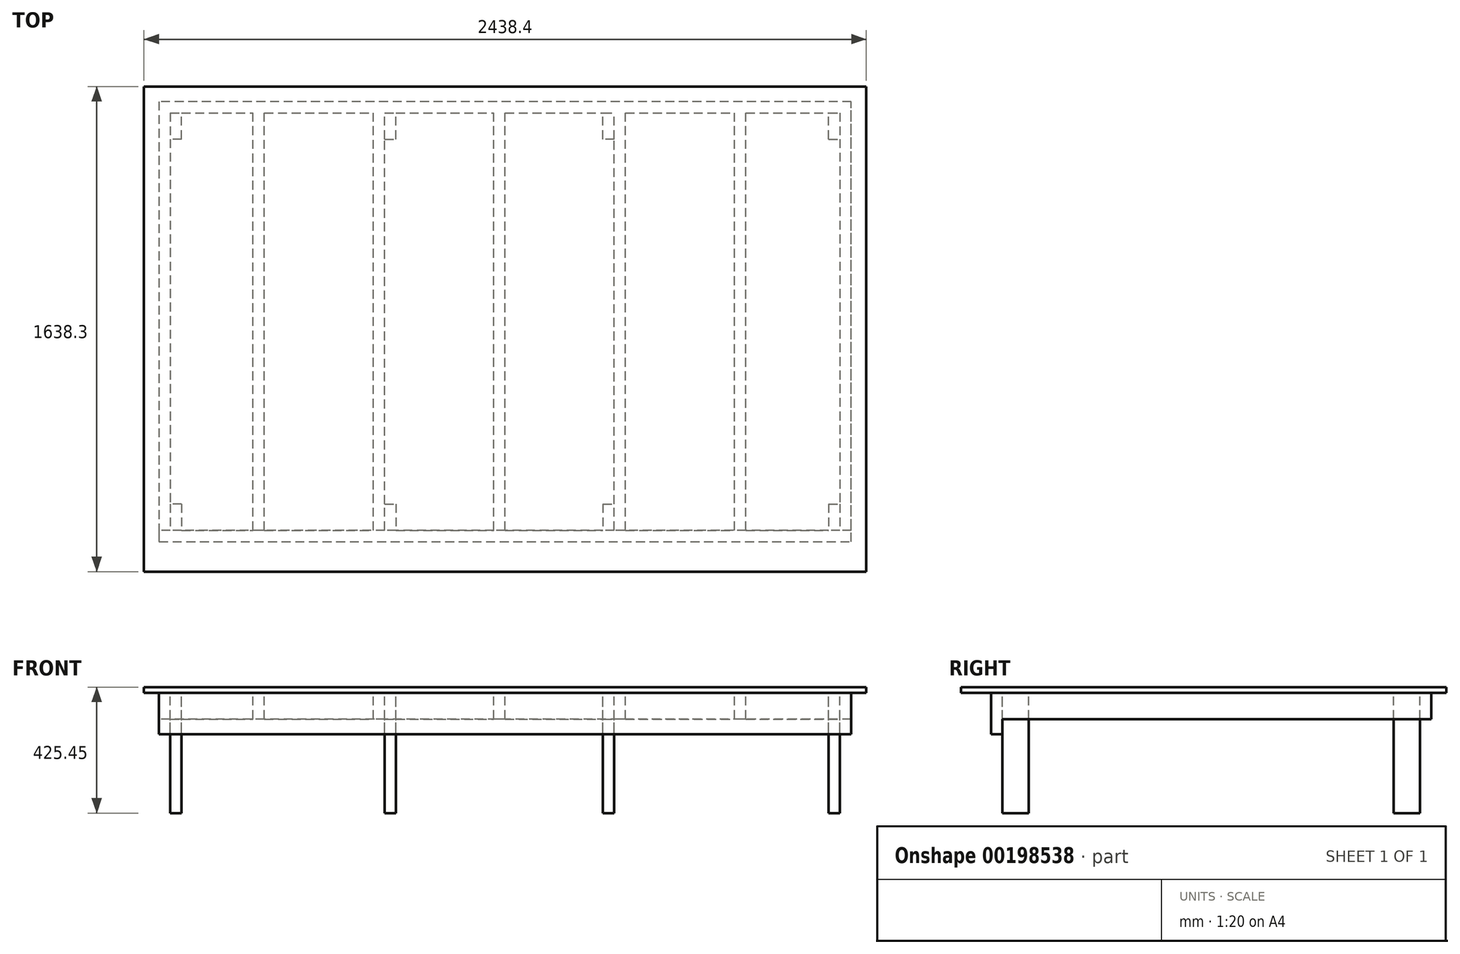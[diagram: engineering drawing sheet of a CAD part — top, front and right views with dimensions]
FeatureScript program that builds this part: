
annotation { "Feature Type Name" : "Feature", "Feature Type Description" : "" }
export const myFeature = defineFeature(function(context is Context, id is Id, definition is map)
    precondition{}
    {
        {
            var Q0;
            Q0=qCreatedBy(makeId("Top.planeOp"),FACE);
            var sketch = newSketch(context, id + "F0", { "sketchPlane" : qUnion([Q0])});
            skLineSegment(sketch, "E0.bottom", {"start": v(0, 0) * mm, "end": v(2438.4, 0) * mm});
            skLineSegment(sketch, "E0.top", {"start": v(0, -1638.3) * mm, "end": v(2438.4, -1638.3) * mm});
            skLineSegment(sketch, "E0.left", {"start": v(0, 0) * mm, "end": v(0, -1638.3) * mm});
            skLineSegment(sketch, "E0.right", {"start": v(2438.4, 0) * mm, "end": v(2438.4, -1638.3) * mm});
            skLineSegment(sketch, "E1", {"start": v(0, -914.4) * mm, "end": v(2438.4, -914.4) * mm});
            skSolve(sketch);
        }
        {
            var Q0;
            Q0 = qSketchRegion(id + "F0", true);
            extrude(context, id + "F1", {"entities" : qUnion([Q0]), "depth" : 19.05 * mm});
        }
        {
            var Q0;
            Q0=makeQuery(id+"F1.opExtrude","CAP_FACE",FACE,{"disambiguationData":[OSD([sQuery(id+"F0.wireOp",EDGE,"E0.bottom"),sQuery(id+"F0.wireOp",EDGE,"E0.top"),sQuery(id+"F0.wireOp",EDGE,"E0.left"),sQuery(id+"F0.wireOp",EDGE,"E0.right")])],"isStart":true});
            var sketch = newSketch(context, id + "F2", { "sketchPlane" : qUnion([Q0])});
            skLineSegment(sketch, "E2.top", {"start": v(88.9, 88.9) * mm, "end": v(368.3, 88.9) * mm});
            skLineSegment(sketch, "E3.top", {"start": v(88.9, 1498.6) * mm, "end": v(368.3, 1498.6) * mm});
            skLineSegment(sketch, "E4", {"start": v(2349.5, 88.9) * mm, "end": v(2349.5, 1498.6) * mm});
            skLineSegment(sketch, "E5", {"start": v(88.9, 88.9) * mm, "end": v(88.9, 1498.6) * mm});
            skLineSegment(sketch, "E6", {"start": v(387.35, 1663.87) * mm, "end": v(387.35, -78) * mm, "construction": true});
            skLineSegment(sketch, "E7", {"start": v(793.75, 1668.2) * mm, "end": v(793.75, -56.39) * mm, "construction": true});
            skLineSegment(sketch, "E8", {"start": v(1200.15, 1668.2) * mm, "end": v(1200.15, -58.55) * mm, "construction": true});
            skLineSegment(sketch, "E9", {"start": v(368.3, 1498.6) * mm, "end": v(368.3, 88.9) * mm});
            skLineSegment(sketch, "E10", {"start": v(774.7, 1498.6) * mm, "end": v(774.7, 88.9) * mm});
            skLineSegment(sketch, "E11.MirrorCS", {"start": v(406.4, 1498.6) * mm, "end": v(406.4, 88.9) * mm});
            skLineSegment(sketch, "E12.MirrorCS", {"start": v(812.8, 1498.6) * mm, "end": v(812.8, 88.9) * mm});
            skLineSegment(sketch, "E13.MirrorCS", {"start": v(1993.9, 1498.6) * mm, "end": v(1993.9, 88.9) * mm});
            skLineSegment(sketch, "E14.MirrorCS", {"start": v(1625.6, 1498.6) * mm, "end": v(1625.6, 88.9) * mm});
            skLineSegment(sketch, "E15.MirrorCS", {"start": v(1587.5, 1498.6) * mm, "end": v(1587.5, 88.9) * mm});
            skLineSegment(sketch, "E16.MirrorCS", {"start": v(2032, 1498.6) * mm, "end": v(2032, 88.9) * mm});
            skLineSegment(sketch, "E17.trimOffspring", {"start": v(1625.6, 1498.6) * mm, "end": v(1993.9, 1498.6) * mm});
            skLineSegment(sketch, "E18.trimOffspring", {"start": v(2032, 1498.6) * mm, "end": v(2349.5, 1498.6) * mm});
            skLineSegment(sketch, "E19.trimOffspring", {"start": v(2032, 88.9) * mm, "end": v(2349.5, 88.9) * mm});
            skLineSegment(sketch, "E20.trimOffspring", {"start": v(1625.6, 88.9) * mm, "end": v(1993.9, 88.9) * mm});
            skLineSegment(sketch, "E21.trimOffspring", {"start": v(812.8, 88.9) * mm, "end": v(1181.1, 88.9) * mm});
            skLineSegment(sketch, "E22.trimOffspring", {"start": v(406.4, 88.9) * mm, "end": v(774.7, 88.9) * mm});
            skLineSegment(sketch, "E23.trimOffspring", {"start": v(406.4, 1498.6) * mm, "end": v(774.7, 1498.6) * mm});
            skLineSegment(sketch, "E24.trimOffspring", {"start": v(812.8, 1498.6) * mm, "end": v(1181.1, 1498.6) * mm});
            skLineSegment(sketch, "E25", {"start": v(1181.1, 1498.6) * mm, "end": v(1181.1, 88.9) * mm});
            skLineSegment(sketch, "E26.MirrorCS", {"start": v(1219.2, 1498.6) * mm, "end": v(1219.2, 88.9) * mm});
            skLineSegment(sketch, "E27.trimOffspring", {"start": v(1219.2, 1498.6) * mm, "end": v(1587.5, 1498.6) * mm});
            skLineSegment(sketch, "E28.trimOffspring", {"start": v(1219.2, 88.9) * mm, "end": v(1587.5, 88.9) * mm});
            skLineSegment(sketch, "E29", {"start": v(50.8, 1536.7) * mm, "end": v(2387.6, 1536.7) * mm});
            skLineSegment(sketch, "E30", {"start": v(2387.6, 1536.7) * mm, "end": v(2387.6, 50.8) * mm});
            skLineSegment(sketch, "E31", {"start": v(2387.6, 50.8) * mm, "end": v(50.8, 50.8) * mm});
            skLineSegment(sketch, "E32", {"start": v(50.8, 50.8) * mm, "end": v(50.8, 1536.7) * mm});
            skSolve(sketch);
        }
        {
            var Q0;
            Q0 = qSketchRegion(id + "F2", true);
            extrude(context, id + "F3", {"entities" : qUnion([Q0]), "operationType" : NewBodyOperationType.ADD, "depth" : 88.9 * mm});
        }
        {
            var Q0;
            Q0=makeQuery(id+"F3.opExtrude","CAP_FACE",FACE,{"disambiguationData":[OSD([sQuery(id+"F2.wireOp",EDGE,"E2.top"),sQuery(id+"F2.wireOp",EDGE,"E3.top"),sQuery(id+"F2.wireOp",EDGE,"E4"),sQuery(id+"F2.wireOp",EDGE,"E5"),sQuery(id+"F2.wireOp",EDGE,"E9"),sQuery(id+"F2.wireOp",EDGE,"E10"),sQuery(id+"F2.wireOp",EDGE,"E11.MirrorCS"),sQuery(id+"F2.wireOp",EDGE,"E12.MirrorCS"),sQuery(id+"F2.wireOp",EDGE,"E13.MirrorCS"),sQuery(id+"F2.wireOp",EDGE,"E14.MirrorCS"),sQuery(id+"F2.wireOp",EDGE,"E15.MirrorCS"),sQuery(id+"F2.wireOp",EDGE,"E16.MirrorCS"),sQuery(id+"F2.wireOp",EDGE,"E17.trimOffspring"),sQuery(id+"F2.wireOp",EDGE,"E18.trimOffspring"),sQuery(id+"F2.wireOp",EDGE,"E19.trimOffspring"),sQuery(id+"F2.wireOp",EDGE,"E20.trimOffspring"),sQuery(id+"F2.wireOp",EDGE,"E21.trimOffspring"),sQuery(id+"F2.wireOp",EDGE,"E22.trimOffspring"),sQuery(id+"F2.wireOp",EDGE,"E23.trimOffspring"),sQuery(id+"F2.wireOp",EDGE,"E24.trimOffspring"),sQuery(id+"F2.wireOp",EDGE,"E26.MirrorCS"),sQuery(id+"F2.wireOp",EDGE,"E25"),sQuery(id+"F2.wireOp",EDGE,"E27.trimOffspring"),sQuery(id+"F2.wireOp",EDGE,"E28.trimOffspring"),sQuery(id+"F2.wireOp",EDGE,"E29"),sQuery(id+"F2.wireOp",EDGE,"E30"),sQuery(id+"F2.wireOp",EDGE,"E31"),sQuery(id+"F2.wireOp",EDGE,"E32")])],"isStart":false});
            var sketch = newSketch(context, id + "F4", { "sketchPlane" : qUnion([Q0])});
            skLineSegment(sketch, "E33.bottom", {"start": v(2387.6, 1536.7) * mm, "end": v(50.8, 1536.7) * mm});
            skLineSegment(sketch, "E33.top", {"start": v(2387.6, 1498.6) * mm, "end": v(50.8, 1498.6) * mm});
            skLineSegment(sketch, "E33.left", {"start": v(2387.6, 1536.7) * mm, "end": v(2387.6, 1498.6) * mm});
            skLineSegment(sketch, "E33.right", {"start": v(50.8, 1536.7) * mm, "end": v(50.8, 1498.6) * mm});
            skSolve(sketch);
        }
        {
            var Q0;
            Q0 = qSketchRegion(id + "F4", true);
            extrude(context, id + "F5", {"entities" : qUnion([Q0]), "operationType" : NewBodyOperationType.ADD, "depth" : 50.8 * mm});
        }
        {
            var Q0;
            Q0=makeQuery(id+"F3.boolean.opBoolean","SPLIT",FACE,{"disambiguationData":[TD([makeQuery(id+"F3.opExtrude","SWEPT_FACE",FACE,{"disambiguationData":[OSD([sQuery(id+"F2.wireOp",EDGE,"E4")])]})])],"derivedFrom":makeQuery(id+"F1.opExtrude","CAP_FACE",FACE,{"disambiguationData":[OSD([sQuery(id+"F0.wireOp",EDGE,"E0.bottom"),sQuery(id+"F0.wireOp",EDGE,"E0.top"),sQuery(id+"F0.wireOp",EDGE,"E0.left"),sQuery(id+"F0.wireOp",EDGE,"E0.right")])],"isStart":true})});
            var sketch = newSketch(context, id + "F6", { "sketchPlane" : qUnion([Q0])});
            skLineSegment(sketch, "E34.bottom", {"start": v(127, 177.8) * mm, "end": v(88.9, 177.8) * mm});
            skLineSegment(sketch, "E34.top", {"start": v(127, 88.9) * mm, "end": v(88.9, 88.9) * mm});
            skLineSegment(sketch, "E34.left", {"start": v(127, 177.8) * mm, "end": v(127, 88.9) * mm});
            skLineSegment(sketch, "E34.right", {"start": v(88.9, 177.8) * mm, "end": v(88.9, 88.9) * mm});
            skLineSegment(sketch, "E35.bottom", {"start": v(2311.4, 177.8) * mm, "end": v(2349.5, 177.8) * mm});
            skLineSegment(sketch, "E35.top", {"start": v(2311.4, 88.9) * mm, "end": v(2349.5, 88.9) * mm});
            skLineSegment(sketch, "E35.left", {"start": v(2311.4, 177.8) * mm, "end": v(2311.4, 88.9) * mm});
            skLineSegment(sketch, "E35.right", {"start": v(2349.5, 177.8) * mm, "end": v(2349.5, 88.9) * mm});
            skLineSegment(sketch, "E36.bottom", {"start": v(2311.4, 1409.7) * mm, "end": v(2349.5, 1409.7) * mm});
            skLineSegment(sketch, "E36.top", {"start": v(2311.4, 1498.6) * mm, "end": v(2349.5, 1498.6) * mm});
            skLineSegment(sketch, "E36.left", {"start": v(2311.4, 1409.7) * mm, "end": v(2311.4, 1498.6) * mm});
            skLineSegment(sketch, "E36.right", {"start": v(2349.5, 1409.7) * mm, "end": v(2349.5, 1498.6) * mm});
            skLineSegment(sketch, "E37.bottom", {"start": v(127, 1409.7) * mm, "end": v(88.9, 1409.7) * mm});
            skLineSegment(sketch, "E37.top", {"start": v(127, 1498.6) * mm, "end": v(88.9, 1498.6) * mm});
            skLineSegment(sketch, "E37.left", {"start": v(127, 1409.7) * mm, "end": v(127, 1498.6) * mm});
            skLineSegment(sketch, "E37.right", {"start": v(88.9, 1409.7) * mm, "end": v(88.9, 1498.6) * mm});
            skLineSegment(sketch, "E38.bottom", {"start": v(812.8, 177.8) * mm, "end": v(850.9, 177.8) * mm});
            skLineSegment(sketch, "E38.top", {"start": v(812.8, 88.9) * mm, "end": v(850.9, 88.9) * mm});
            skLineSegment(sketch, "E38.left", {"start": v(850.9, 177.8) * mm, "end": v(850.9, 88.9) * mm});
            skLineSegment(sketch, "E38.right", {"start": v(812.8, 177.8) * mm, "end": v(812.8, 88.9) * mm});
            skLineSegment(sketch, "E39.bottom", {"start": v(1587.5, 177.8) * mm, "end": v(1549.4, 177.8) * mm});
            skLineSegment(sketch, "E39.top", {"start": v(1587.5, 88.9) * mm, "end": v(1549.4, 88.9) * mm});
            skLineSegment(sketch, "E39.left", {"start": v(1587.5, 177.8) * mm, "end": v(1587.5, 88.9) * mm});
            skLineSegment(sketch, "E39.right", {"start": v(1549.4, 177.8) * mm, "end": v(1549.4, 88.9) * mm});
            skLineSegment(sketch, "E40.bottom", {"start": v(1549.4, 1409.7) * mm, "end": v(1587.5, 1409.7) * mm});
            skLineSegment(sketch, "E40.top", {"start": v(1549.4, 1498.6) * mm, "end": v(1587.5, 1498.6) * mm});
            skLineSegment(sketch, "E40.left", {"start": v(1549.4, 1409.7) * mm, "end": v(1549.4, 1498.6) * mm});
            skLineSegment(sketch, "E40.right", {"start": v(1587.5, 1409.7) * mm, "end": v(1587.5, 1498.6) * mm});
            skLineSegment(sketch, "E41.bottom", {"start": v(812.8, 1409.7) * mm, "end": v(850.9, 1409.7) * mm});
            skLineSegment(sketch, "E41.top", {"start": v(812.8, 1498.6) * mm, "end": v(850.9, 1498.6) * mm});
            skLineSegment(sketch, "E41.left", {"start": v(812.8, 1409.7) * mm, "end": v(812.8, 1498.6) * mm});
            skLineSegment(sketch, "E41.right", {"start": v(850.9, 1409.7) * mm, "end": v(850.9, 1498.6) * mm});
            skSolve(sketch);
        }
        {
            var Q0;
            Q0 = qSketchRegion(id + "F6", true);
            extrude(context, id + "F7", {"entities" : qUnion([Q0]), "operationType" : NewBodyOperationType.ADD, "depth" : 406.4 * mm});
        }
    });
